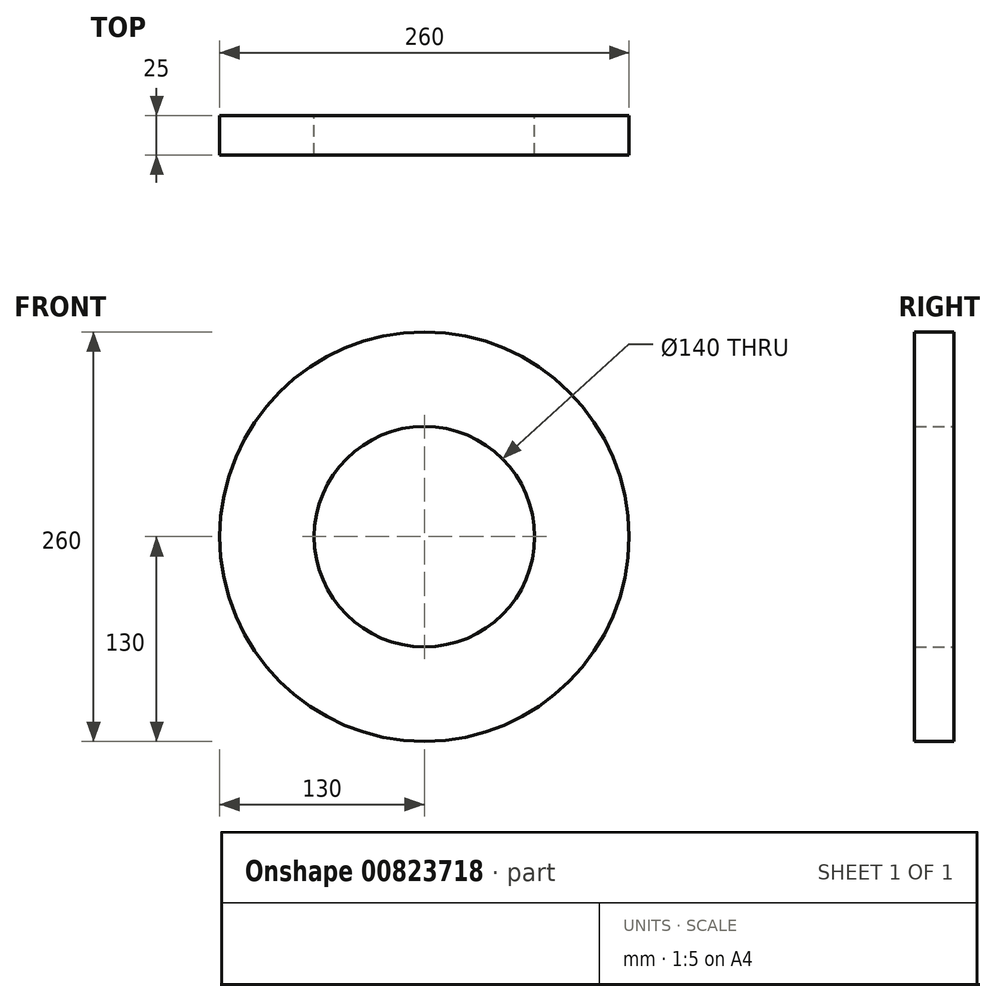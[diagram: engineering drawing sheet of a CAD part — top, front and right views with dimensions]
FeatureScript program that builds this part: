
annotation { "Feature Type Name" : "Feature", "Feature Type Description" : "" }
export const myFeature = defineFeature(function(context is Context, id is Id, definition is map)
    precondition{}
    {
        {
            var Q0;
            Q0=qCreatedBy(makeId("Front.planeOp"),FACE);
            var sketch = newSketch(context, id + "F0", { "sketchPlane" : qUnion([Q0])});
            skCircle(sketch, "E0", {"center": v(0, 0) * mm, "radius": 130 * mm});
            skCircle(sketch, "E1", {"center": v(0, 0) * mm, "radius": 70 * mm});
            skSolve(sketch);
        }
        {
            var Q0;
            Q0 = qSketchRegion(id + "F0", true);
            extrude(context, id + "F1", {"entities" : qUnion([Q0]), "depth" : 25 * mm, "offsetDistance" : 25 * mm});
        }
    });
